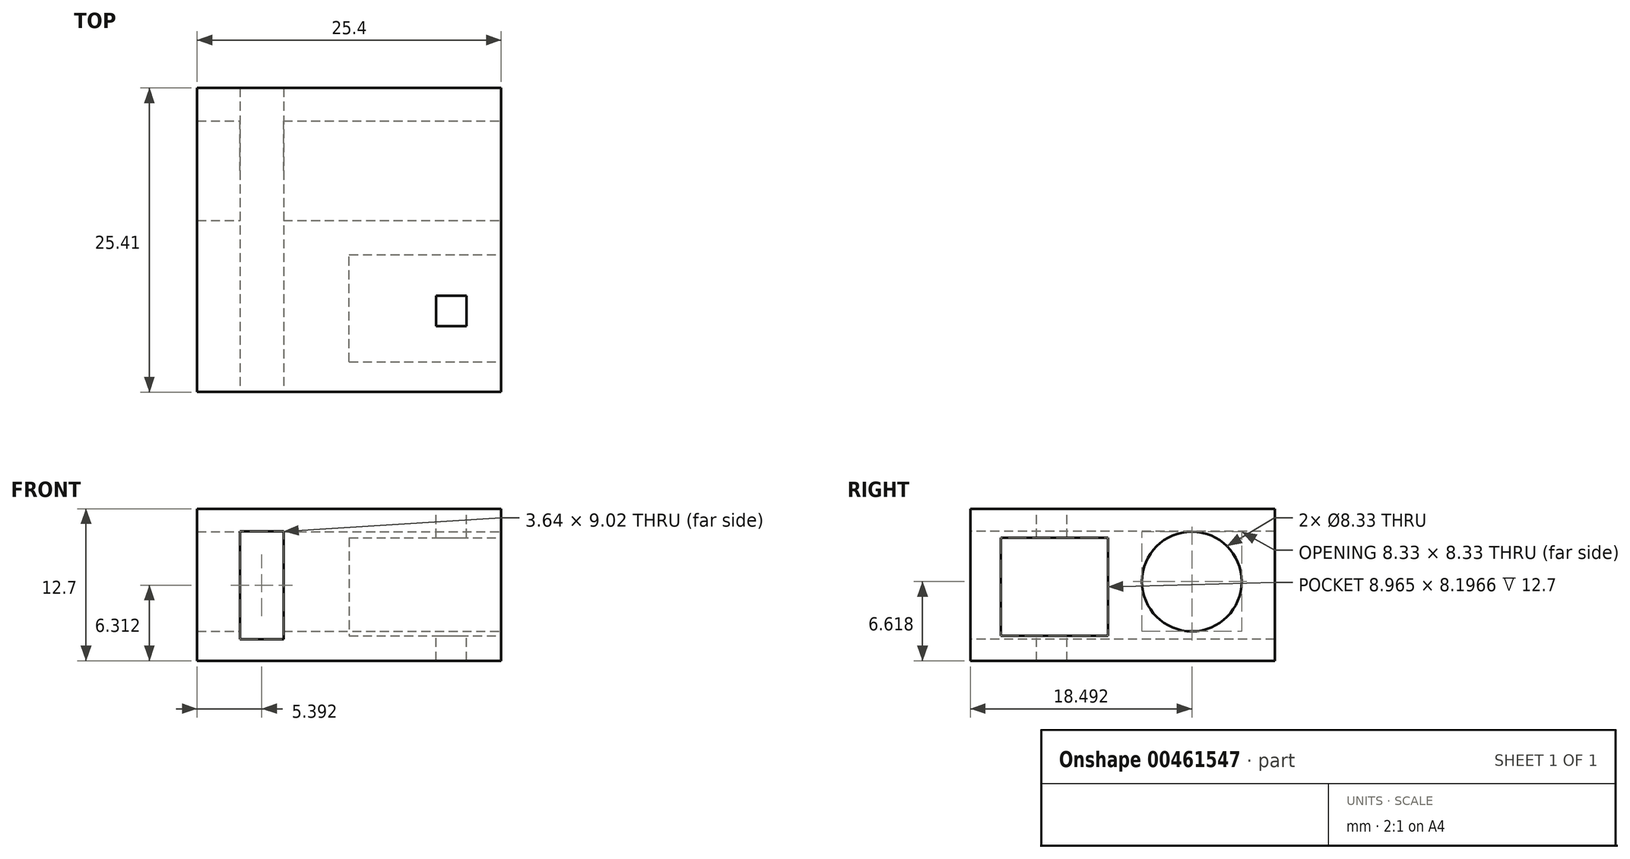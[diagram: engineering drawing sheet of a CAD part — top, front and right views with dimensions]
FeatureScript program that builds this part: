
annotation { "Feature Type Name" : "Feature", "Feature Type Description" : "" }
export const myFeature = defineFeature(function(context is Context, id is Id, definition is map)
    precondition{}
    {
        {
            var Q0;
            Q0=qCreatedBy(makeId("Top.planeOp"),FACE);
            var sketch = newSketch(context, id + "F0", { "sketchPlane" : qUnion([Q0])});
            skLineSegment(sketch, "E0.bottom", {"start": v(-56.6, -31.65) * mm, "end": v(-31.2, -31.65) * mm});
            skLineSegment(sketch, "E0.top", {"start": v(-56.6, -57.06) * mm, "end": v(-31.2, -57.06) * mm});
            skLineSegment(sketch, "E0.left", {"start": v(-56.6, -31.65) * mm, "end": v(-56.6, -57.06) * mm});
            skLineSegment(sketch, "E0.right", {"start": v(-31.2, -31.65) * mm, "end": v(-31.2, -57.06) * mm});
            skSolve(sketch);
        }
        {
            var Q0;
            Q0=makeQuery(id+"F0.imprint","IMPRINT",FACE,{"disambiguationData":[TD([[makeQuery(id+"F0.imprint","IMPRINT",EDGE,{"derivedFrom":sQuery(id+"F0.wireOp",EDGE,"E0.bottom")}),-1.0]])]});
            extrude(context, id + "F1", {"entities" : qUnion([Q0]), "depth" : 12.7 * mm});
        }
        {
            var Q0;
            Q0=makeQuery(id+"F1.opExtrude","SWEPT_FACE",FACE,{"disambiguationData":[OSD([sQuery(id+"F0.wireOp",EDGE,"E0.right")])]});
            var sketch = newSketch(context, id + "F2", { "sketchPlane" : qUnion([Q0])});
            skLineSegment(sketch, "E1.bottom", {"start": v(-54.54, 10.28) * mm, "end": v(-45.57, 10.28) * mm});
            skLineSegment(sketch, "E1.top", {"start": v(-54.54, 2.08) * mm, "end": v(-45.57, 2.08) * mm});
            skLineSegment(sketch, "E1.left", {"start": v(-54.54, 10.28) * mm, "end": v(-54.54, 2.08) * mm});
            skLineSegment(sketch, "E1.right", {"start": v(-45.57, 10.28) * mm, "end": v(-45.57, 2.08) * mm});
            skSolve(sketch);
        }
        {
            var Q0;
            Q0=makeQuery(id+"F2.imprint","IMPRINT",FACE,{"disambiguationData":[TD([[makeQuery(id+"F2.imprint","IMPRINT",EDGE,{"derivedFrom":sQuery(id+"F2.wireOp",EDGE,"E1.bottom")}),-1.0]])]});
            extrude(context, id + "F3", {"entities" : qUnion([Q0]), "operationType" : NewBodyOperationType.REMOVE, "oppositeDirection" : true, "depth" : 12.7 * mm});
        }
        {
            var Q0;
            Q0=makeQuery(id+"F1.opExtrude","SWEPT_FACE",FACE,{"disambiguationData":[OSD([sQuery(id+"F0.wireOp",EDGE,"E0.right")])]});
            var sketch = newSketch(context, id + "F4", { "sketchPlane" : qUnion([Q0])});
            skCircle(sketch, "E2", {"center": v(-38.57, 6.62) * mm, "radius": 4.16 * mm});
            skSolve(sketch);
        }
        {
            var Q0;
            Q0=makeQuery(id+"F4.imprint","IMPRINT",FACE,{"disambiguationData":[TD([[makeQuery(id+"F4.imprint","IMPRINT",EDGE,{"derivedFrom":sQuery(id+"F4.wireOp",EDGE,"E2")}),1.0]])]});
            extrude(context, id + "F5", {"entities" : qUnion([Q0]), "operationType" : NewBodyOperationType.REMOVE, "oppositeDirection" : true, "depth" : 25.4 * mm});
        }
        {
            var Q0;
            Q0=makeQuery(id+"F1.opExtrude","SWEPT_FACE",FACE,{"disambiguationData":[OSD([sQuery(id+"F0.wireOp",EDGE,"E0.top")])]});
            var sketch = newSketch(context, id + "F6", { "sketchPlane" : qUnion([Q0])});
            skLineSegment(sketch, "E3.bottom", {"start": v(-53.03, 10.82) * mm, "end": v(-49.39, 10.82) * mm});
            skLineSegment(sketch, "E3.top", {"start": v(-53.03, 1.8) * mm, "end": v(-49.39, 1.8) * mm});
            skLineSegment(sketch, "E3.left", {"start": v(-53.03, 10.82) * mm, "end": v(-53.03, 1.8) * mm});
            skLineSegment(sketch, "E3.right", {"start": v(-49.39, 10.82) * mm, "end": v(-49.39, 1.8) * mm});
            skSolve(sketch);
        }
        {
            var Q0;
            Q0=makeQuery(id+"F6.imprint","IMPRINT",FACE,{"disambiguationData":[TD([[makeQuery(id+"F6.imprint","IMPRINT",EDGE,{"derivedFrom":sQuery(id+"F6.wireOp",EDGE,"E3.bottom")}),-1.0]])]});
            extrude(context, id + "F7", {"entities" : qUnion([Q0]), "operationType" : NewBodyOperationType.REMOVE, "oppositeDirection" : true, "depth" : 25.4 * mm});
        }
        {
            var Q0;
            Q0=makeQuery(id+"F1.opExtrude","CAP_FACE",FACE,{"disambiguationData":[OSD([sQuery(id+"F0.wireOp",EDGE,"E0.bottom"),sQuery(id+"F0.wireOp",EDGE,"E0.top"),sQuery(id+"F0.wireOp",EDGE,"E0.left"),sQuery(id+"F0.wireOp",EDGE,"E0.right")])],"isStart":false});
            var sketch = newSketch(context, id + "F8", { "sketchPlane" : qUnion([Q0])});
            skLineSegment(sketch, "E4.bottom", {"start": v(-34.1, -49) * mm, "end": v(-36.65, -49) * mm});
            skLineSegment(sketch, "E4.top", {"start": v(-34.1, -51.55) * mm, "end": v(-36.65, -51.55) * mm});
            skLineSegment(sketch, "E4.left", {"start": v(-34.1, -49) * mm, "end": v(-34.1, -51.55) * mm});
            skLineSegment(sketch, "E4.right", {"start": v(-36.65, -49) * mm, "end": v(-36.65, -51.55) * mm});
            skSolve(sketch);
        }
        {
            var Q0;
            Q0=makeQuery(id+"F8.imprint","IMPRINT",FACE,{"disambiguationData":[TD([[makeQuery(id+"F8.imprint","IMPRINT",EDGE,{"derivedFrom":sQuery(id+"F8.wireOp",EDGE,"E4.bottom")}),1.0]])]});
            var sketch = newSketch(context, id + "F9", { "sketchPlane" : qUnion([Q0])});
            skSolve(sketch);
        }
        {
            var Q0;
            Q0 = qSketchRegion(id + "F9", true);
            var Q1;
            Q1=makeQuery(id+"F8.imprint","IMPRINT",FACE,{"disambiguationData":[TD([[makeQuery(id+"F8.imprint","IMPRINT",EDGE,{"derivedFrom":sQuery(id+"F8.wireOp",EDGE,"E4.bottom")}),1.0]])]});
            extrude(context, id + "F10", {"entities" : qUnion([Q0, Q1]), "operationType" : NewBodyOperationType.REMOVE, "oppositeDirection" : true, "depth" : 25.4 * mm});
        }
    });
